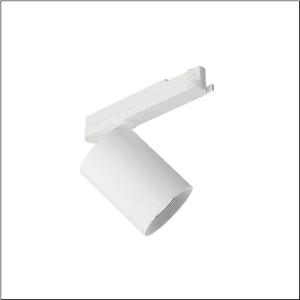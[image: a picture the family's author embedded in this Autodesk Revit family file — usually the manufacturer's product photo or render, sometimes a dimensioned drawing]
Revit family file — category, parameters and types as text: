
# Revit family: spot_21_51se14mba5b
name_source: partatom
category: Lighting Fixtures
units: mm (PartAtom-declared; Revit-internal decimal feet)

## family parameters
Cut with Voids When Loaded = No
Host = Face
Light Source = No
Part Type = Normal
Room Calculation Point = No
Round Connector Dimension = Use Diameter
Shared = No

## types (1)
- --- (1 x LED, 5340 lm, 41.8 W, 2700K)
    Apparent Load = 42 VA
    CIE Flux Codes = 96 99 100 100 100
    Color Rendering = 90
    Color Temperature = 2700K
    Default Elevation = 1800 mm
    Description = Spot 21, directional spotlight, light control with lens, of PMMA, LED rated luminous flux: 5.030lm, light colour: 927, control gear: ECG Multilumen, with 3-phase adapter, mains connection: 220..240V, AC, 50/60Hz, of aluminium, traffic white (RAL 9016), length: 213mm, diameter: 105mm, protection rating (complete): IP20, insulation class (complete): insulation class I (protective earthing), certification: CE, impact resistance: IK02, permissible ambient temperature for indoor applications: -20..+40°C, packaging unit: 1 piece
    Height = 175 mm
    Lamp = 1 x LED
    Lamp Light Flux = 5340 lm
    Lamp Power = 41.8 W
    Lamp count = 1
    Length = 105 mm
    Luminous efficacy = 128 lm/W
    Manufacturer = Siteco
    ModVariant = No
    Model = 51SE14MBA5B
    Mounting Place = Ceiling
    Mounting Type = Pendant
    Number of Poles = 1
    OnlyDefault = Yes
    Power Factor = 1
    Product Name = Spot 21
    Product group = directional spotlight
    ProductGroupID = 905
    Protection Class = Protection class I
    Protection Degree = IP 20
    RLX_Detail_Level = 1
    RLX_Emergency_Light_Flux = 0 lm
    RLX_Emergency_Type = 0
    RLX_Emergency_Type_DB = No
    RlxData = <blob elided: 17637 chars, md5=4d20266c>
    Socket = socket
    Standby Power = 0 W
    System Light Flux = 5340 lm
    System Power = 42 W
    Type Comments = factory setting: luminous flux: 100 % | (ON | ON | ON | ON) | 1050 mA
    Type Image = l_1003976.jpg
    URL = http://relux.com
    VarID = @adj_092945
    Voltage = 0 V
    Weight = 0.00 kg
    Width = 0 mm  [stored 0 ft]

note: [stored X ft] marks values corroborated as IEEE doubles in the binary element streams (Revit-internal decimal feet)

## geometry (parser evidence)
native form markers: Blend x4, Sweep x10
no freeform markers — native parametric forms only
